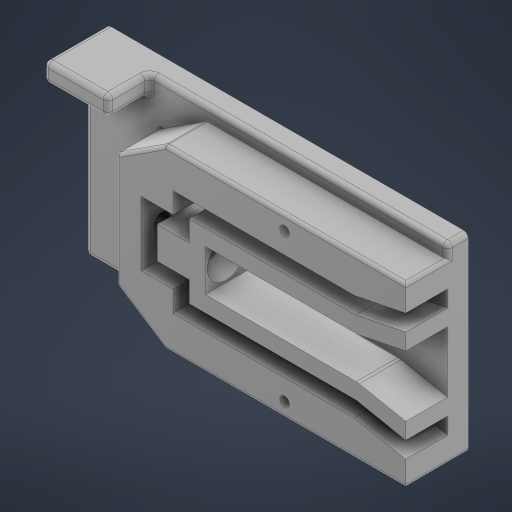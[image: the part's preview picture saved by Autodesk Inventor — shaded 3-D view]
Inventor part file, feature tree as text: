
AUTODESK INVENTOR PART (.ipt)
format: ipt  version: 2024.1 (Build 281209000, 209)  size: 4,699,136 bytes
history: native  units: mm
features: sketch x10, extrude x7, other x3, fillet x3, projected_geometry x3, plane x2, hole x2, revolve x1
ambient origin geometry x8: Origin, YZ Plane, XZ Plane, XY Plane, X Axis, Y Axis, Z Axis, Center Point
bodies: Solid1 (feature_tree)
feature tree (31):
  other  "3D_PCB1_2024-08-12"
  plane  "Work Plane1"
  extrude  "Extrusion1"  Depth=10.0mm
  extrude  "Extrusion2"  Depth=10.0mm
  extrude  "Extrusion3"  Depth=1.5mm
  fillet  "Fillet1"  Radius=1.5mm
  extrude  "Extrusion6"  Depth=1.5mm
  hole  "Hole1"  [1 undecoded]
  extrude  "Extrusion5"  TaperAngle=0.0deg  [1 undecoded]
  fillet  "Fillet2"  Radius=3.0mm
  extrude  "Extrusion7"  Depth=0.3mm
  extrude  "Extrusion8"  Depth=13.0mm
  fillet  "Fillet3"  Radius=47.5mm
  plane  "Work Plane3"
  revolve  "Revolution1"  [1 undecoded]
  hole  "Hole2"  [1 undecoded]
  sketch  "Sketch2"  dims[d0=10.0mm d1=10.0mm]
  sketch  "Sketch3"  dims[d2=10.0mm d3=10.0mm]
  sketch  "Sketch6"  dims[d4=1.5mm d5=1.5mm d6=1.5mm]
  sketch  "Sketch8"  dims[d7=1.5mm d8=1.5mm]
  sketch  "Sketch10"  dims[d9=1.5mm d10=1.5mm]
  sketch  "Sketch11"  dims[d11=3.51mm d12=0.0mm d13=0.0mm d14=3.0mm d15=0.0mm]
  sketch  "Sketch12"  dims[d19=0.3mm d20=0.3mm]
  projected_geometry  "Projected Loop4"
  sketch  "Sketch13"  dims[d21=0.3mm d22=13.0mm d23=47.5mm]
  sketch  "Sketch14"  dims[d24=3.0mm d25=5.0mm]
  other  "Work Point1"
  sketch  "Sketch17"  dims[d26=13.0mm d27=0.0mm d28=5.0mm d29=10.0mm d30=10.0mm d31=5.0mm d32=6.0mm d33=4.0mm d34=2.0mm d35=90.0deg d36=8.0mm d37=20.594885mm d41=0.0mm d42=0.0mm d43=5.0mm d44=5.0mm d46=5.0mm d49=10.0mm d50=0.0mm d52=1.0mm d53=1.0mm d54=3.0mm d55=4.0mm d56=0.0mm d57=3.0mm d58=3.0mm d59=1.0mm d60=1.0mm d61=1.0mm d62=0.5mm d63=0.5mm d64=37.718mm d65=46.0mm d66=3.0mm d67=6.0mm d68=4.0mm d69=2.0mm d70=90.0deg d71=8.0mm d72=20.594885mm d73=16.5mm d74=16.5mm d75=20.0mm d76=27.0mm d77=0.0mm d78=1.5mm d79=6.0mm d80=1.98176mm d81=1.98176mm d85=5.4mm d86=5.9mm d87=90.0deg]
  projected_geometry  "Projected Loop6"
  other  "3D_PCB1_2024-08-12.obj"
  projected_geometry  "Project Cut Edges2"
note: 4 required parameter values undecoded (feature->parameter linkage not recoverable at this tier; creation-order binding heuristic only, values carry confidence <= 0.55)